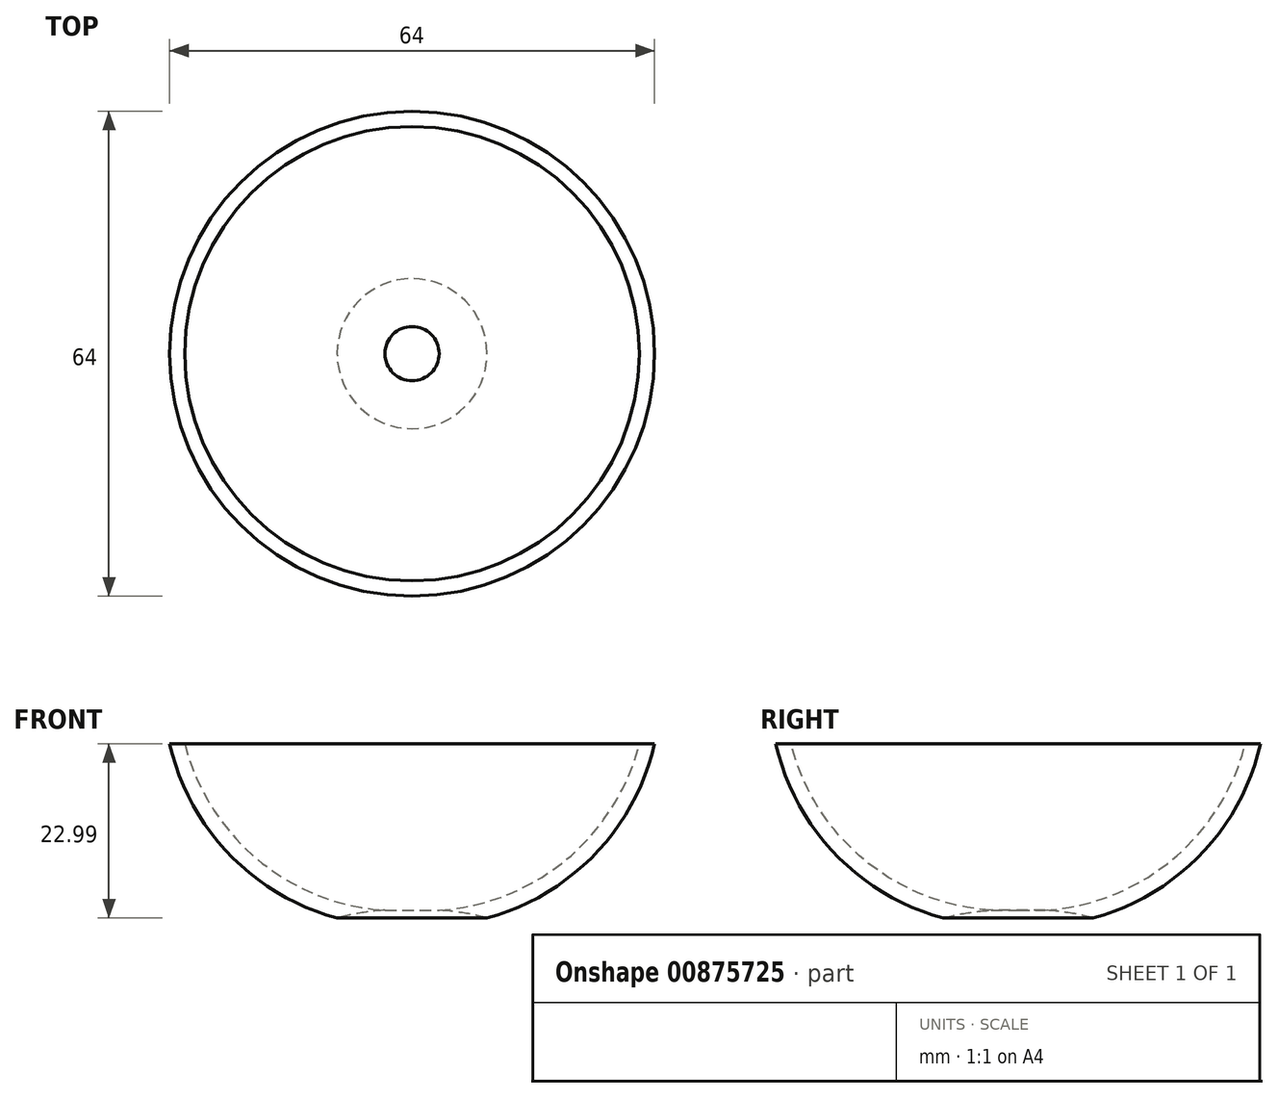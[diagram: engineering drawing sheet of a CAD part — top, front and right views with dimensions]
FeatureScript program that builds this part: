
annotation { "Feature Type Name" : "Feature", "Feature Type Description" : "" }
export const myFeature = defineFeature(function(context is Context, id is Id, definition is map)
    precondition{}
    {
        {
            var Q0;
            Q0=qCreatedBy(makeId("Right.planeOp"),FACE);
            var sketch = newSketch(context, id + "F0", { "sketchPlane" : qUnion([Q0])});
            skLineSegment(sketch, "E0", {"start": v(-32, 24) * mm, "end": v(-30, 24) * mm});
            skLineSegment(sketch, "E1", {"start": v(0, 0) * mm, "end": v(0, 2) * mm});
            skLineSegment(sketch, "E2", {"start": v(-30, 24) * mm, "end": v(0, 24) * mm});
            skLineSegment(sketch, "E3", {"start": v(0, 2) * mm, "end": v(0, 24) * mm});
            skArc(sketch, "E4", {"start": v(-32, 24) * mm, "mid": v(-20.4, 6.13) * mm, "end": v(0, 0) * mm});
            skArc(sketch, "E5", {"start": v(-30, 24) * mm, "mid": v(-18.95, 7.61) * mm, "end": v(0, 2) * mm});
            skLineSegment(sketch, "E6", {"start": v(0, 0) * mm, "end": v(0, -22) * mm});
            skLineSegment(sketch, "E7", {"start": v(0, -22) * mm, "end": v(-30, -22) * mm});
            skArc(sketch, "E8", {"start": v(0, 0) * mm, "mid": v(-18.99, -5.56) * mm, "end": v(-30, -22) * mm});
            skLineSegment(sketch, "E9", {"start": v(-30, -22) * mm, "end": v(-32, -22) * mm});
            skArc(sketch, "E10", {"start": v(0, 2) * mm, "mid": v(-20.42, -4.1) * mm, "end": v(-32, -22) * mm});
            skSolve(sketch);
        }
        {
            var Q0;
            Q0=makeQuery(id+"F0.imprint","IMPRINT",FACE,{"disambiguationData":[TD([[makeQuery(id+"F0.imprint","IMPRINT",EDGE,{"derivedFrom":sQuery(id+"F0.wireOp",EDGE,"E0")}),-1.0]])]});
            var Q1;
            Q1=sQuery(id+"F0.wireOp",EDGE,"E1");
            revolve(context, id + "F1", {"surfaceOperationType" : NewSurfaceOperationType.NEW, "entities" : qUnion([Q0]), "axis" : qUnion([Q1]), "revolveType" : RevolveType.FULL});
        }
    });
